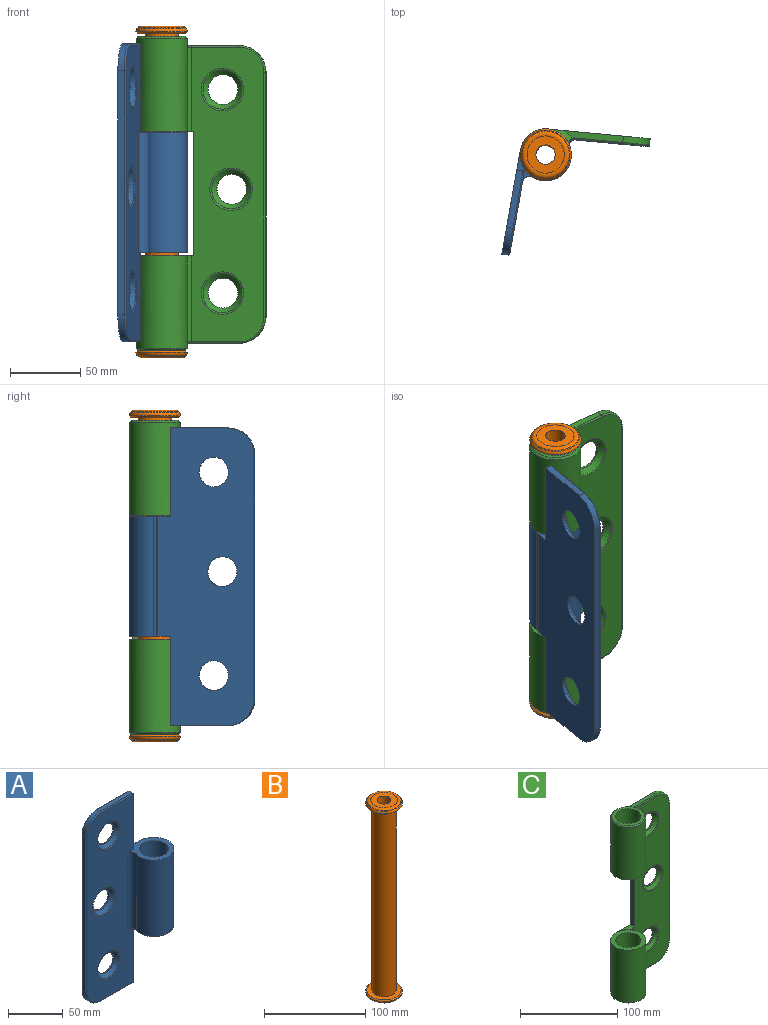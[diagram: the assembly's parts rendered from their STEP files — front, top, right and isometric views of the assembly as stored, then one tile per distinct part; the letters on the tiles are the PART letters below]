
ASSEMBLY  parts=3 mates=2
PART A: 30 faces, bbox 94.3x36.3x214.4 mm
  f0: plane 63.58x5.51mm, normal (1,0,0), area 350.3mm2, adj f1,f2,f5,f10,f24
  f1: plane 209.2x59.34mm, normal (0,-1,0), area 9467.4mm2, adj f0,f3,f7,f10,f20,f21,f22,f24
  f2: plane 211.24x69.08mm, normal (0,1,0), area 12284.3mm2, adj f0,f3,f4,f5,f6,f7,f10,f11
  f3: plane 40.06x36.32mm, normal (0,0,1), area 542.1mm2, adj f1,f2,f7,f8,f9,f19,f23,f29
  f4: plane 41.31x4.5mm, normal (0,0,1), area 185.7mm2, adj f2,f7,f17,f26
  f5: plane 41.31x4.5mm, normal (0,0,-1), area 185.7mm2, adj f0,f2,f18,f24
  f6: plane 173.14x4.5mm, normal (-1,0,0), area 778.5mm2, adj f2,f17,f18,f27
  f7: plane 62.49x5.51mm, normal (1,0,0), area 344.2mm2, adj f1,f2,f3,f4,f26
  f8: cylinder r=18.13mm len=85.17mm, axis (0,0,-1), area 8001mm2, adj f3,f10,f19,f29
  f9: cylinder r=13.05mm len=85.17mm, axis (0,0,-1), area 6982.2mm2, adj f3,f10
  f10: plane 40.06x36.32mm, normal (0,0,-1), area 542.1mm2, adj f0,f1,f2,f8,f9,f19,f23,f29
  f11: cylinder r=10.57mm len=21.14mm, axis (0,1,0), area 113.1mm2, adj f2,f16
  f12: cylinder r=10.57mm len=21.14mm, axis (0,1,0), area 113.1mm2, adj f2,f14
  f13: cylinder r=10.57mm len=21.14mm, axis (0,1,0), area 113.1mm2, adj f2,f15
  f14: cone r=10.57mm half-angle=45deg, axis (0,-1,0), area 357mm2, adj f12,f20
  f15: cone r=10.57mm half-angle=45deg, axis (0,-1,0), area 357mm2, adj f13,f21
  f16: cone r=10.57mm half-angle=45deg, axis (0,-1,0), area 357mm2, adj f11,f22
  f17: cylinder r=19.05mm len=19.05mm, axis (0,1,0), area 134.5mm2, adj f2,f4,f6,f28
  f18: cylinder r=19.05mm len=19.05mm, axis (0,-1,0), area 134.5mm2, adj f2,f5,f6,f25
  f19: cylinder r=5.08mm len=85.17mm, axis (0,0,1), area 160.8mm2, adj f3,f8,f10,f23
  f20: torus R=15.12mm, axis (0,1,0), area 126.8mm2, adj f1,f14
  f21: torus R=15.12mm, axis (0,1,0), area 126.8mm2, adj f1,f15
  f22: torus R=15.12mm, axis (0,1,0), area 126.8mm2, adj f1,f16
  f23: cylinder r=5.08mm len=85.17mm, axis (0,0,1), area 101.8mm2, adj f2,f3,f10,f19
  f24: cylinder r=1.02mm len=41.31mm, axis (-1,0,0), area 65.9mm2, adj f0,f1,f5,f25
  f25: torus R=18.03mm, axis (0,1,0), area 46.8mm2, adj f1,f18,f24,f27
  f26: cylinder r=1.02mm len=41.31mm, axis (1,0,0), area 65.9mm2, adj f1,f4,f7,f28
  f27: cylinder r=1.02mm len=173.14mm, axis (0,0,-1), area 276.3mm2, adj f1,f6,f25,f28
  f28: torus R=18.03mm, axis (0,1,0), area 46.8mm2, adj f1,f17,f26,f27
  f29: cylinder r=5.08mm len=85.17mm, axis (0,0,-1), area 824mm2, adj f1,f3,f8,f10
PART B: 14 faces, bbox 39.6x39.6x235.4 mm
  f0: plane 34.02x34.02mm, normal (0,0,1), area 460.9mm2, adj f2,f13
  f1: plane 34.04x34.04mm, normal (0,0,-1), area 462mm2, adj f2,f12
  f2: cylinder r=11.94mm len=224.96mm, axis (0,0,-1), area 16878.6mm2, adj f0,f1
  f3: plane 26.42x26.42mm, normal (0,0,-1), area 400.4mm2, adj f5,f10
  f4: plane 26.42x26.42mm, normal (0,0,1), area 400.4mm2, adj f5,f11
  f5: cylinder r=6.86mm len=235.12mm, axis (0,0,-1), area 10136.2mm2, adj f3,f4
  f6: cone r=18.29mm half-angle=45deg, axis (0,0,1), area 92.3mm2, adj f9,f10
  f7: cone r=13.21mm half-angle=45deg, axis (0,0,-1), area 76.4mm2, adj f8,f11
  f8: torus R=14.74mm, axis (0,0,1), area 296.3mm2, adj f7,f12
  f9: torus R=14.74mm, axis (0,0,-1), area 271.7mm2, adj f6,f13
  f10: torus R=14.12mm, axis (0,0,-1), area 350.2mm2, adj f3,f6
  f11: torus R=14.23mm, axis (0,0,1), area 361.9mm2, adj f4,f7
  f12: cone r=18.29mm half-angle=43.7deg, axis (0,0,1), area 203.7mm2, adj f1,f8
  f13: cone r=17.01mm half-angle=42deg, axis (0,0,-1), area 209.3mm2, adj f0,f9
PART C: 46 faces, bbox 92.5x44.5x224.3 mm
  f0: cylinder r=18.13mm len=66.14mm, axis (0,0,-1), area 6342.7mm2, adj f1,f12,f13,f14,f45
  f1: plane 39.34x36.32mm, normal (0,0,-1), area 575.1mm2, adj f0,f2,f3,f4,f7,f12,f13,f32
  f2: cylinder r=13.05mm len=67.41mm, axis (0,0,-1), area 5526.8mm2, adj f1,f43
  f3: plane 209.2x51.69mm, normal (0,-1,0), area 8420mm2, adj f1,f7,f8,f13,f16,f28,f29,f30
  f4: plane 214.2x67.57mm, normal (0,1,0), area 11655.5mm2, adj f1,f5,f6,f7,f8,f14,f18,f19
  f5: plane 41.47x5.15mm, normal (0,0,1), area 175mm2, adj f4,f14,f26,f38,f40
  f6: plane 41.47x5.15mm, normal (0,0,-1), area 175mm2, adj f4,f18,f27,f34,f35
  f7: plane 88.47x5.51mm, normal (-1,0,0), area 487.7mm2, adj f1,f3,f4,f8
  f8: plane 17.06x9.25mm, normal (0,0,1), area 70.5mm2, adj f3,f4,f7,f15,f16,f31
  f9: cylinder r=18.13mm len=65.85mm, axis (0,0,-1), area 6288.6mm2, adj f10,f16,f17,f18,f44
  f10: plane 36.26x36.26mm, normal (0,0,1), area 497.5mm2, adj f9,f11,f15
  f11: cylinder r=13.05mm len=67.12mm, axis (0,0,-1), area 5502.7mm2, adj f10,f42
  f12: cylinder r=3.81mm len=64.65mm, axis (0,0,-1), area 94.1mm2, adj f0,f1,f14,f32
  f13: cylinder r=3.81mm len=64.65mm, axis (0,0,-1), area 462.3mm2, adj f0,f1,f3,f36,f38
  f14: torus R=21.94mm, axis (0,0,-1), area 75.7mm2, adj f0,f4,f5,f12,f32,f36
  f15: torus R=18.55mm, axis (0,0,1), area 7mm2, adj f8,f10,f16,f17,f31
  f16: cylinder r=3.81mm len=65.77mm, axis (0,0,-1), area 470.7mm2, adj f3,f8,f9,f15,f33,f34
  f17: cylinder r=3.81mm len=65.77mm, axis (0,0,1), area 95.8mm2, adj f9,f15,f18,f31
  f18: torus R=21.94mm, axis (0,0,-1), area 75.7mm2, adj f4,f6,f9,f17,f31,f33
  f19: plane 173.14x4.5mm, normal (1,0,0), area 778.5mm2, adj f4,f26,f27,f39
  f20: cylinder r=10.57mm len=21.14mm, axis (0,1,0), area 113.1mm2, adj f4,f25
  f21: cylinder r=10.57mm len=21.14mm, axis (0,1,0), area 113.1mm2, adj f4,f24
  f22: cylinder r=10.57mm len=21.14mm, axis (0,1,0), area 113.1mm2, adj f4,f23
  f23: cone r=14.38mm half-angle=45deg, axis (0,-1,0), area 357mm2, adj f22,f28
  f24: cone r=14.38mm half-angle=45deg, axis (0,-1,0), area 357mm2, adj f21,f29
  f25: cone r=14.38mm half-angle=45deg, axis (0,-1,0), area 357mm2, adj f20,f30
  f26: cylinder r=19.05mm len=19.05mm, axis (0,-1,0), area 134.5mm2, adj f4,f5,f19,f41
  f27: cylinder r=19.05mm len=19.05mm, axis (0,1,0), area 134.5mm2, adj f4,f6,f19,f37
  f28: torus R=15.12mm, axis (0,-1,0), area 126.8mm2, adj f3,f23
  f29: torus R=15.12mm, axis (0,-1,0), area 126.8mm2, adj f3,f24
  f30: torus R=15.12mm, axis (0,-1,0), area 126.8mm2, adj f3,f25
  f31: cylinder r=5.08mm len=64.18mm, axis (0,0,1), area 80.5mm2, adj f4,f8,f15,f17,f18
  f32: cylinder r=5.08mm len=63.08mm, axis (0,0,-1), area 79.2mm2, adj f1,f4,f12,f14
  f33: bspline ~5.98x4.83mm, area 6.8mm2, adj f16,f18,f34
  f34: torus R=4.83mm, axis (0,0,-1), area 3.5mm2, adj f6,f16,f33,f35
  f35: cylinder r=1.02mm len=33.66mm, axis (-1,0,0), area 53.7mm2, adj f3,f6,f34,f37
  f36: bspline ~5.98x4.83mm, area 6.8mm2, adj f13,f14,f38
  f37: torus R=18.03mm, axis (0,-1,0), area 46.8mm2, adj f3,f27,f35,f39
  f38: torus R=4.83mm, axis (0,0,-1), area 3.5mm2, adj f5,f13,f36,f40
  f39: cylinder r=1.02mm len=173.14mm, axis (0,0,-1), area 276.3mm2, adj f3,f19,f37,f41
  f40: cylinder r=1.02mm len=33.66mm, axis (1,0,0), area 53.7mm2, adj f3,f5,f38,f41
  f41: torus R=18.03mm, axis (0,-1,0), area 46.8mm2, adj f3,f26,f39,f40
  f42: plane 33.72x33.72mm, normal (0,0,-1), area 358mm2, adj f11,f44
  f43: plane 33.72x33.72mm, normal (0,0,1), area 358mm2, adj f2,f45
  f44: cone r=18.13mm half-angle=45deg, axis (0,0,1), area 197.4mm2, adj f9,f42
  f45: cone r=16.86mm half-angle=45deg, axis (0,0,-1), area 197.4mm2, adj f0,f43
PLACE A rot(axis=(0,0,1),79.9deg) t=(-176.92,41.47,16.46)mm
PLACE B t=(-103.24,46.69,16.26)mm
PLACE C rot(axis=(0,0,-1),5.4deg) t=(-99.18,43.09,15.3)mm
MATE revolute C.f0 <-> B.f2  axis (0,0,1) through (-137.17,0.04,-140.26)mm
MATE revolute A.f8 <-> B.f2  axis (0,0,-1) through (-137.17,0.04,-27.78)mm
